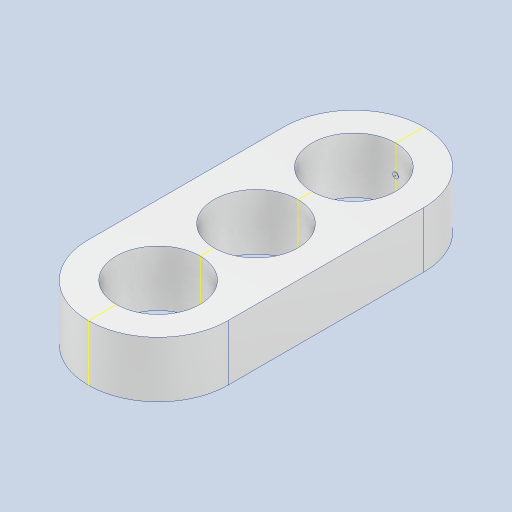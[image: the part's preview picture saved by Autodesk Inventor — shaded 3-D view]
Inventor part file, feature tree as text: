
AUTODESK INVENTOR PART (.ipt)
format: ipt  version: 2024 (Build 280153000, 153)  size: 359,936 bytes
history: native  units: mm
features: sketch x4, other x4, extrude x3, plane x3
ambient origin geometry x8: Origin, YZ Plane, XZ Plane, XY Plane, X Axis, Y Axis, Z Axis, Center Point
bodies: Body1 (feature_tree)
feature tree (14):
  extrude  "Extrusión3"  Depth=10.0mm
  plane  "Plano de trabajo1"
  sketch  "Boceto2"  dims[d12=30.0mm d13=20.0mm d14=0.0mm]
  other  "Punto de trabajo1"
  other  "Punto de trabajo2"
  plane  "Plano de trabajo2"
  plane  "Plano de trabajo3"
  extrude  "Extrusión4"  Depth=20.0mm TaperAngle=0.0deg
  extrude  "Extrusión5"  Depth=2.0mm
  sketch  "Boceto1"  dims[d3=10.0mm d6=0.0mm]
  sketch  "Boceto3"  dims[d15=-25.0mm d16=2.0mm]
  sketch  "Boceto4"  dims[d17=0.1mm d18=0.0mm d19=2.0mm d20=0.1mm d21=0.0mm d22=14.3117mm d23=0.75mm d24=20.594885mm d25=0.0625mm d26=0.75mm d27=0.375mm]
  other  "Proyectar aristas de corte1"
  other  "Proyectar aristas de corte2"
